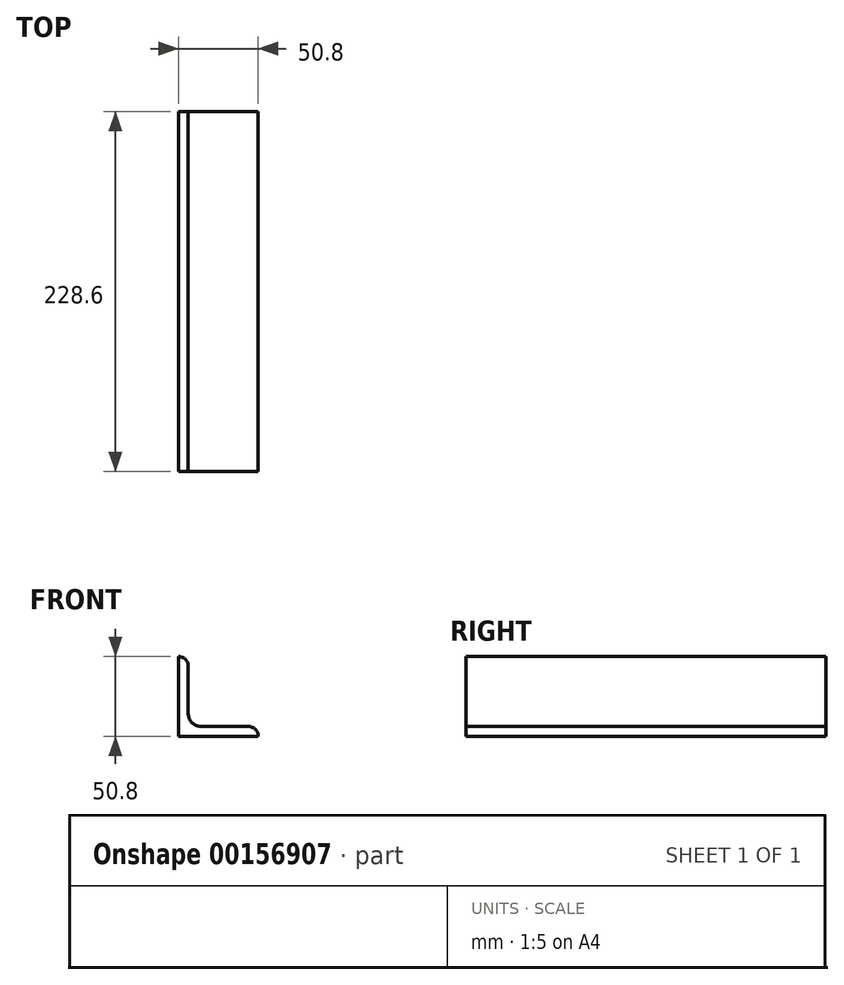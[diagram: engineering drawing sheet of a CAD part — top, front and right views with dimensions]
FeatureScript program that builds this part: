
annotation { "Feature Type Name" : "Feature", "Feature Type Description" : "" }
export const myFeature = defineFeature(function(context is Context, id is Id, definition is map)
    precondition{}
    {
        {
            var Q0;
            Q0=qCreatedBy(makeId("Front.planeOp"),FACE);
            var sketch = newSketch(context, id + "F0", { "sketchPlane" : qUnion([Q0])});
            skLineSegment(sketch, "E0", {"start": v(0, 0) * mm, "end": v(0, 50.8) * mm});
            skLineSegment(sketch, "E1", {"start": v(0, 0) * mm, "end": v(50.8, 0) * mm});
            skLineSegment(sketch, "E2.0", {"start": v(6.35, 14.29) * mm, "end": v(6.35, 44.45) * mm});
            skLineSegment(sketch, "E3.0", {"start": v(14.29, 6.35) * mm, "end": v(44.45, 6.35) * mm});
            skLineSegment(sketch, "E4", {"start": v(0, 50.8) * mm, "end": v(0, 50.8) * mm});
            skLineSegment(sketch, "E5", {"start": v(50.8, 0) * mm, "end": v(50.8, 0) * mm});
            skPoint(sketch, "E6.visualSharp", {"position": v(6.35, 6.35) * mm});
            skArc(sketch, "E6.filletArc", {"start": v(6.35, 14.29) * mm, "mid": v(8.67, 8.67) * mm, "end": v(14.29, 6.35) * mm});
            skPoint(sketch, "E7.visualSharp", {"position": v(6.35, 50.8) * mm});
            skArc(sketch, "E7.filletArc", {"start": v(6.35, 44.45) * mm, "mid": v(4.5, 48.94) * mm, "end": v(0, 50.8) * mm});
            skPoint(sketch, "E8.visualSharp", {"position": v(50.8, 6.35) * mm});
            skArc(sketch, "E8.filletArc", {"start": v(50.8, 0) * mm, "mid": v(48.94, 4.5) * mm, "end": v(44.45, 6.35) * mm});
            skSolve(sketch);
        }
        {
            var Q0;
            Q0=makeQuery(id+"F0.imprint","IMPRINT",FACE,{"disambiguationData":[TD([[makeQuery(id+"F0.imprint","IMPRINT",EDGE,{"derivedFrom":sQuery(id+"F0.wireOp",EDGE,"E0")}),-1.0]])]});
            extrude(context, id + "F1", {"entities" : qUnion([Q0]), "depth" : 228.6 * mm});
        }
    });
